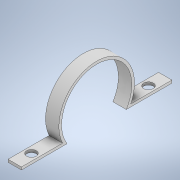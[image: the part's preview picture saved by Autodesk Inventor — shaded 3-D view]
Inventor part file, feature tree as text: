
AUTODESK INVENTOR PART (.ipt)
format: ipt  version: 2021 (Build 250183000, 183)  size: 131,072 bytes
history: native  units: in
note: dims shown in document units (in); Inventor stores cm internally (conversion verified against a paired STEP export)
features: extrude x2, sketch x2
ambient origin geometry x8: Origin, YZ Plane, XZ Plane, XY Plane, X Axis, Y Axis, Z Axis, Center Point
bodies: Body1 (feature_tree)
feature tree (4):
  extrude  "Extrusion5"  Depth=1.6535in
  extrude  "Extrusion6"  Depth=3.5433in
  sketch  "Sketch9"  dims[d26=1.378in d36=1.6535in]
  sketch  "Sketch10"  dims[d37=1.7795in d38=3.5433in d39=1.7717in d40=0.063in d41=0.315in d42=0.0in d43=0.2283in d44=0.2283in d45=0.3937in d46=0.3937in d47=0.1575in d48=0.1575in d49=0.0in d50=0.0in d7=0.0197in d8=0.0344in d9=0.0197in d10=0.0344in]
